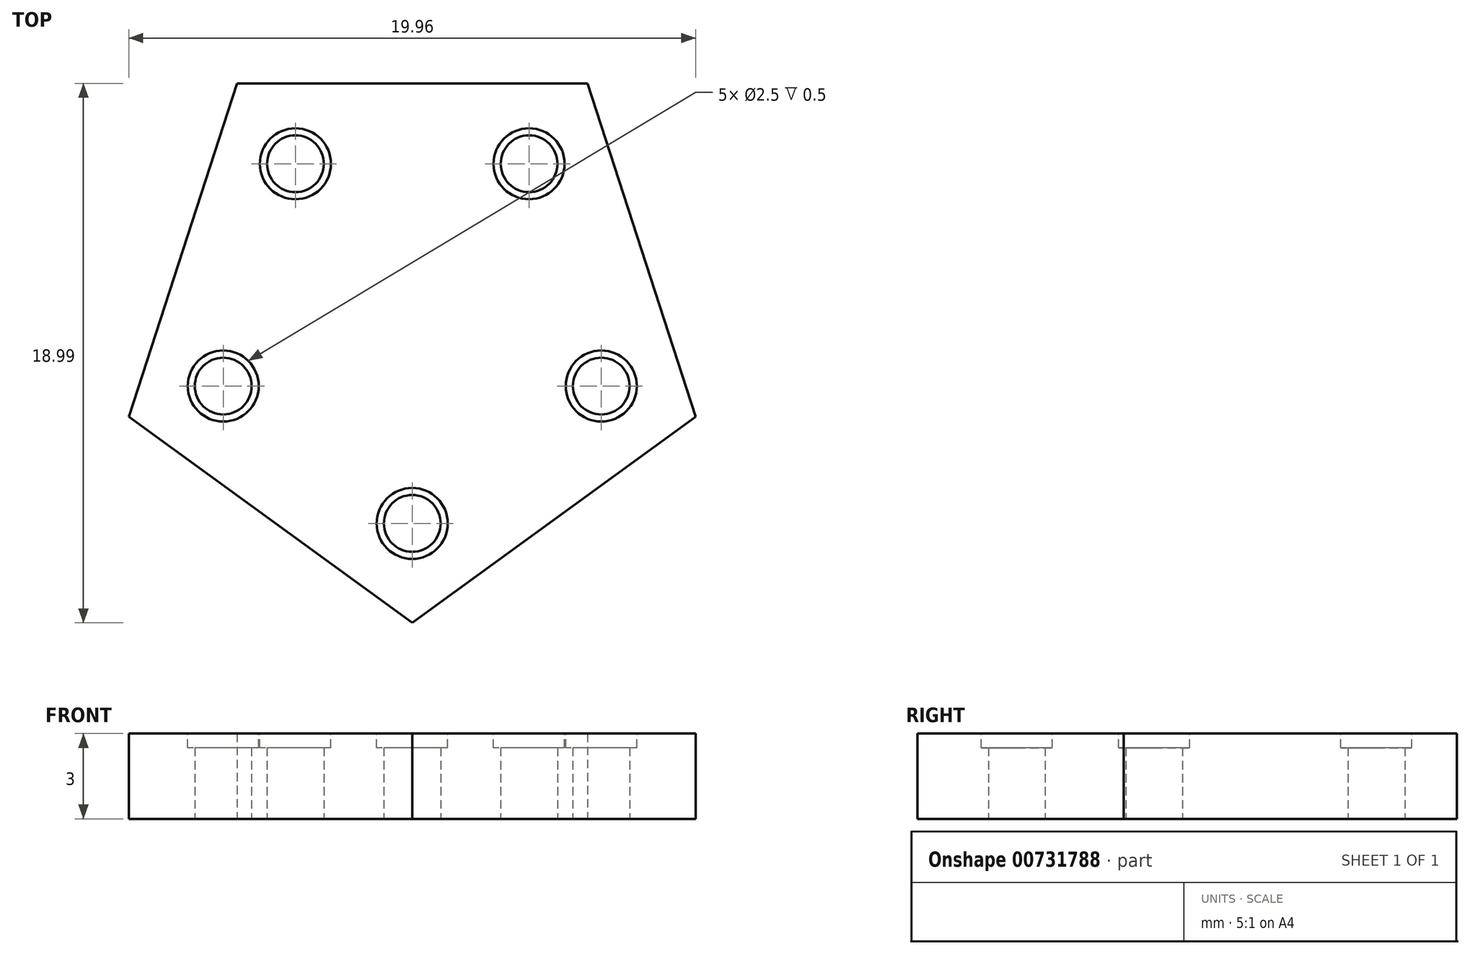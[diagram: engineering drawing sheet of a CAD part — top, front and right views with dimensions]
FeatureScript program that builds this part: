
annotation { "Feature Type Name" : "Feature", "Feature Type Description" : "" }
export const myFeature = defineFeature(function(context is Context, id is Id, definition is map)
    precondition{}
    {
        {
            var Q0;
            Q0=qCreatedBy(makeId("Top.planeOp"),FACE);
            var sketch = newSketch(context, id + "F0", { "sketchPlane" : qUnion([Q0])});
            skCircle(sketch, "E0.cCircle", {"center": v(0, 0) * mm, "radius": 8.5 * mm, "construction": true});
            skLineSegment(sketch, "E0.0", {"start": v(-6.17, 8.5) * mm, "end": v(6.17, 8.5) * mm});
            skLineSegment(sketch, "E0.1", {"start": v(6.17, 8.5) * mm, "end": v(9.98, -3.24) * mm});
            skLineSegment(sketch, "E0.2", {"start": v(9.98, -3.24) * mm, "end": v(0, -10.5) * mm});
            skLineSegment(sketch, "E0.3", {"start": v(0, -10.5) * mm, "end": v(-9.98, -3.24) * mm});
            skLineSegment(sketch, "E0.4", {"start": v(-9.98, -3.24) * mm, "end": v(-6.17, 8.5) * mm});
            skPoint(sketch, "E0.0.midPoint", {"position": v(0, 8.5) * mm});
            skCircle(sketch, "E1", {"center": v(0, 0) * mm, "radius": 7 * mm, "construction": true});
            skLineSegment(sketch, "E2", {"start": v(0, 0) * mm, "end": v(0, -12.96) * mm, "construction": true});
            skCircle(sketch, "E3", {"center": v(0, -7) * mm, "radius": 1 * mm});
            skCircle(sketch, "E4.1.0", {"center": v(6.66, -2.16) * mm, "radius": 1 * mm});
            skCircle(sketch, "E4.2.0", {"center": v(4.11, 5.66) * mm, "radius": 1 * mm});
            skCircle(sketch, "E4.3.0", {"center": v(-4.11, 5.66) * mm, "radius": 1 * mm});
            skCircle(sketch, "E4.4.0", {"center": v(-6.66, -2.16) * mm, "radius": 1 * mm});
            skLineSegment(sketch, "E5", {"start": v(0, 0) * mm, "end": v(-9.98, -3.24) * mm, "construction": true});
            skLineSegment(sketch, "E6", {"start": v(0, 0) * mm, "end": v(9.98, -3.24) * mm, "construction": true});
            skLineSegment(sketch, "E7", {"start": v(0, 0) * mm, "end": v(6.17, 8.5) * mm, "construction": true});
            skLineSegment(sketch, "E8", {"start": v(0, 0) * mm, "end": v(-6.17, 8.5) * mm, "construction": true});
            skSolve(sketch);
        }
        {
            var Q0;
            Q0=makeQuery(id+"F0.imprint","IMPRINT",FACE,{"disambiguationData":[TD([[makeQuery(id+"F0.imprint","IMPRINT",EDGE,{"derivedFrom":sQuery(id+"F0.wireOp",EDGE,"E0.0")}),-1.0]])]});
            extrude(context, id + "F1", {"entities" : qUnion([Q0]), "depth" : 3 * mm, "offsetDistance" : 25 * mm});
        }
        {
            var Q0;
            Q0=makeQuery(id+"F1.opExtrude","CAP_FACE",FACE,{"disambiguationData":[OSD([sQuery(id+"F0.wireOp",EDGE,"E0.0"),sQuery(id+"F0.wireOp",EDGE,"E0.1"),sQuery(id+"F0.wireOp",EDGE,"E0.2"),sQuery(id+"F0.wireOp",EDGE,"E0.3"),sQuery(id+"F0.wireOp",EDGE,"E0.4"),sQuery(id+"F0.wireOp",EDGE,"E3"),sQuery(id+"F0.wireOp",EDGE,"E4.1.0"),sQuery(id+"F0.wireOp",EDGE,"E4.2.0"),sQuery(id+"F0.wireOp",EDGE,"E4.3.0"),sQuery(id+"F0.wireOp",EDGE,"E4.4.0")])],"isStart":false});
            var sketch = newSketch(context, id + "F2", { "sketchPlane" : qUnion([Q0])});
            skCircle(sketch, "E9", {"center": v(0, -7) * mm, "radius": 1.25 * mm});
            skCircle(sketch, "E10.1.0", {"center": v(6.66, -2.16) * mm, "radius": 1.25 * mm});
            skCircle(sketch, "E10.2.0", {"center": v(4.11, 5.66) * mm, "radius": 1.25 * mm});
            skCircle(sketch, "E10.3.0", {"center": v(-4.11, 5.66) * mm, "radius": 1.25 * mm});
            skCircle(sketch, "E10.4.0", {"center": v(-6.66, -2.16) * mm, "radius": 1.25 * mm});
            skPoint(sketch, "E10.center", {"position": v(0, 0) * mm});
            skSolve(sketch);
        }
        {
            var Q0;
            Q0 = qSketchRegion(id + "F2", true);
            extrude(context, id + "F3", {"entities" : qUnion([Q0]), "operationType" : NewBodyOperationType.REMOVE, "oppositeDirection" : true, "depth" : 0.5 * mm, "offsetDistance" : 25 * mm});
        }
        {
            var Q0;
            Q0=makeQuery(id+"F1.opExtrude","CAP_FACE",FACE,{"disambiguationData":[OSD([sQuery(id+"F0.wireOp",EDGE,"E0.0"),sQuery(id+"F0.wireOp",EDGE,"E0.1"),sQuery(id+"F0.wireOp",EDGE,"E0.2"),sQuery(id+"F0.wireOp",EDGE,"E0.3"),sQuery(id+"F0.wireOp",EDGE,"E0.4"),sQuery(id+"F0.wireOp",EDGE,"E3"),sQuery(id+"F0.wireOp",EDGE,"E4.1.0"),sQuery(id+"F0.wireOp",EDGE,"E4.2.0"),sQuery(id+"F0.wireOp",EDGE,"E4.3.0"),sQuery(id+"F0.wireOp",EDGE,"E4.4.0")])],"isStart":false});
            cPlane(context, id + "F4", {"entities" : qUnion([Q0]), "cplaneType" : CPlaneType.OFFSET, "offset" : 1.5 * mm, "oppositeDirection" : true, "width" : 150 * mm, "height" : 150 * mm});
        }
    });
